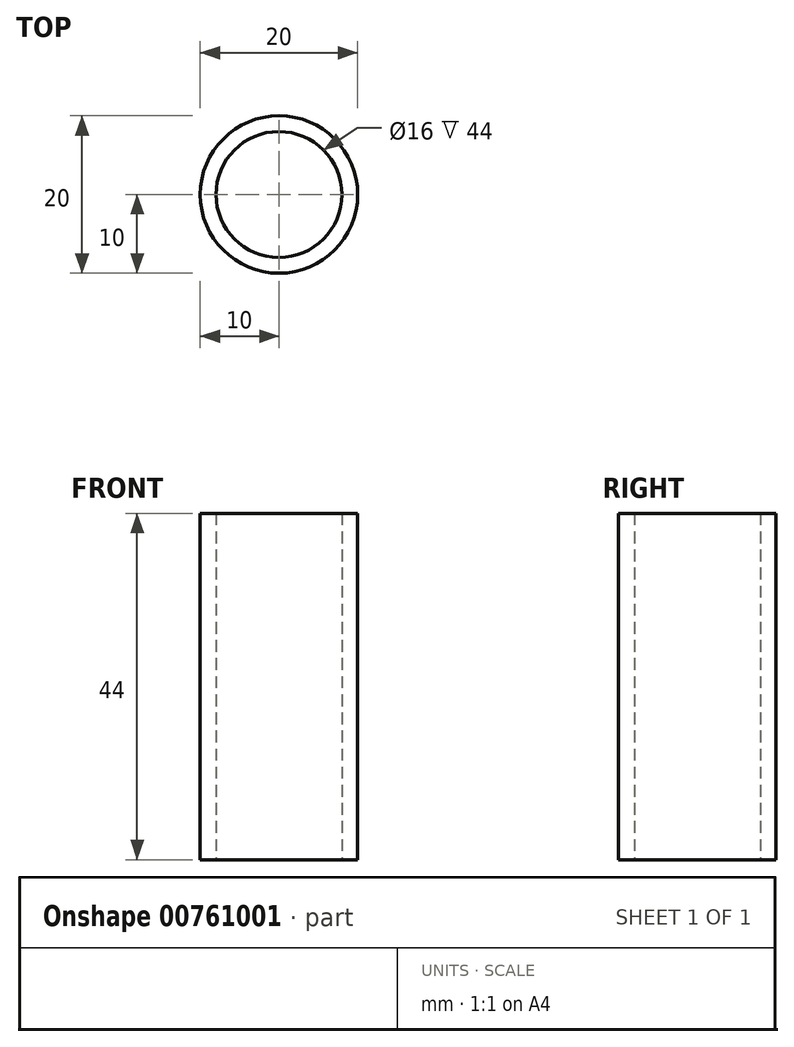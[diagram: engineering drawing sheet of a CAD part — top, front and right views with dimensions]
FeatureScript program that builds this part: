
annotation { "Feature Type Name" : "Feature", "Feature Type Description" : "" }
export const myFeature = defineFeature(function(context is Context, id is Id, definition is map)
    precondition{}
    {
        {
            var Q0;
            Q0=qCreatedBy(makeId("Top.planeOp"),FACE);
            var sketch = newSketch(context, id + "F0", { "sketchPlane" : qUnion([Q0])});
            skCircle(sketch, "E0", {"center": v(0, 0) * mm, "radius": 8 * mm});
            skCircle(sketch, "E1", {"center": v(0, 0) * mm, "radius": 10 * mm});
            skSolve(sketch);
        }
        {
            var Q0;
            Q0 = qSketchRegion(id + "F0", true);
            extrude(context, id + "F1", {"entities" : qUnion([Q0]), "depth" : 44 * mm, "offsetDistance" : 25 * mm});
        }
    });
